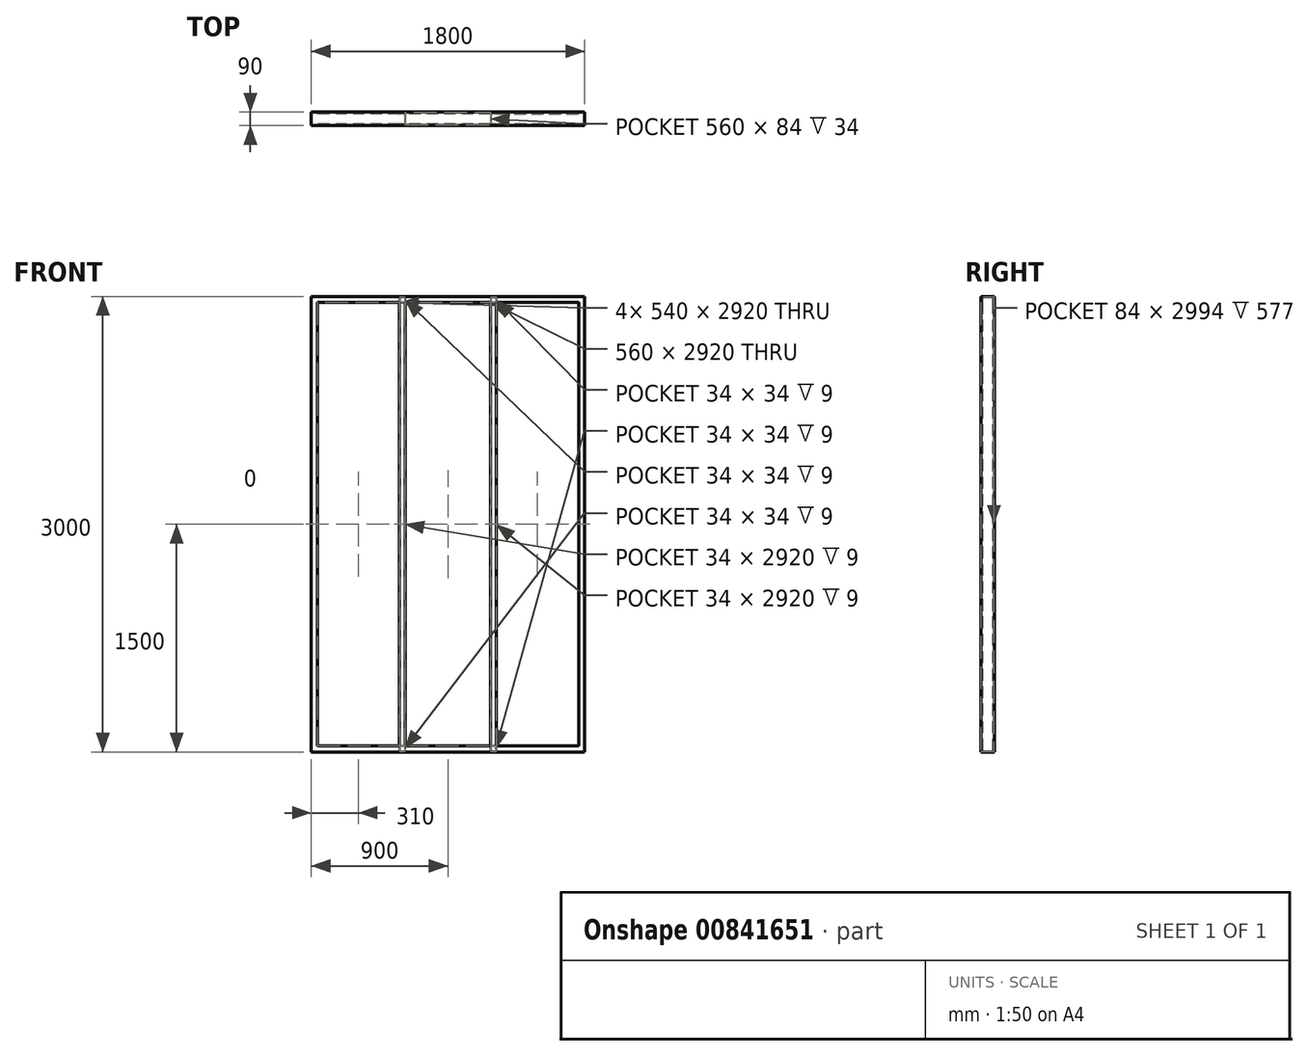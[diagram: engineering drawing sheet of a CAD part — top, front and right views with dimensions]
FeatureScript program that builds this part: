
annotation { "Feature Type Name" : "Feature", "Feature Type Description" : "" }
export const myFeature = defineFeature(function(context is Context, id is Id, definition is map)
    precondition{}
    {
        {
            var Q0;
            Q0=qCreatedBy(makeId("Front.planeOp"),FACE);
            var sketch = newSketch(context, id + "F0", { "sketchPlane" : qUnion([Q0])});
            skLineSegment(sketch, "E0.bottom", {"start": v(0, 0) * mm, "end": v(1800, 0) * mm});
            skLineSegment(sketch, "E0.top", {"start": v(0, 3000) * mm, "end": v(1800, 3000) * mm});
            skLineSegment(sketch, "E0.left", {"start": v(0, 0) * mm, "end": v(0, 3000) * mm});
            skLineSegment(sketch, "E0.right", {"start": v(1800, 0) * mm, "end": v(1800, 3000) * mm});
            skSolve(sketch);
        }
        {
            var Q0;
            Q0=qCreatedBy(makeId("Top.planeOp"),FACE);
            var sketch = newSketch(context, id + "F1", { "sketchPlane" : qUnion([Q0])});
            skLineSegment(sketch, "E1", {"start": v(0, 0) * mm, "end": v(0, -45) * mm});
            skLineSegment(sketch, "E2", {"start": v(0, -45) * mm, "end": v(40, -45) * mm});
            skLineSegment(sketch, "E3", {"start": v(40, -45) * mm, "end": v(40, -33) * mm});
            skLineSegment(sketch, "E4.MirrorCS", {"start": v(0, 0) * mm, "end": v(0, 45) * mm});
            skLineSegment(sketch, "E5.MirrorCS", {"start": v(0, 45) * mm, "end": v(40, 45) * mm});
            skLineSegment(sketch, "E6.MirrorCS", {"start": v(40, 45) * mm, "end": v(40, 33) * mm});
            skLineSegment(sketch, "E7.0", {"start": v(37, 42) * mm, "end": v(37, 33) * mm});
            skLineSegment(sketch, "E7.1", {"start": v(3, 42) * mm, "end": v(37, 42) * mm});
            skLineSegment(sketch, "E7.2", {"start": v(37, -42) * mm, "end": v(37, -33) * mm});
            skLineSegment(sketch, "E7.3", {"start": v(3, -42) * mm, "end": v(37, -42) * mm});
            skLineSegment(sketch, "E7.4", {"start": v(3, 0) * mm, "end": v(3, -42) * mm});
            skLineSegment(sketch, "E7.5", {"start": v(3, 0) * mm, "end": v(3, 42) * mm});
            skLineSegment(sketch, "E8", {"start": v(37, 33) * mm, "end": v(40, 33) * mm});
            skLineSegment(sketch, "E9", {"start": v(37, -33) * mm, "end": v(40, -33) * mm});
            skSolve(sketch);
        }
        {
            var Q0;
            Q0 = qSketchRegion(id + "F1", true);
            var Q1;
            Q1 = qConstructionFilter(qBodyType(qCreatedBy(id + "F0" ,EDGE), BodyType.WIRE), ConstructionObject.NO);
            sweep(context, id + "F2", {"profiles" : qUnion([Q0]), "path" : qUnion([Q1])});
        }
        {
            var Q0;
            Q0=qCreatedBy(makeId("Top.planeOp"),FACE);
            var sketch = newSketch(context, id + "F3", { "sketchPlane" : qUnion([Q0])});
            skLineSegment(sketch, "E10", {"start": v(580, -45) * mm, "end": v(620, -45) * mm});
            skLineSegment(sketch, "E11", {"start": v(620, -45) * mm, "end": v(620, 45) * mm});
            skLineSegment(sketch, "E12", {"start": v(620, 45) * mm, "end": v(580, 45) * mm});
            skLineSegment(sketch, "E13", {"start": v(580, 45) * mm, "end": v(580, 33) * mm});
            skLineSegment(sketch, "E14", {"start": v(580, -45) * mm, "end": v(580, -33) * mm});
            skLineSegment(sketch, "E15", {"start": v(900, -276.13) * mm, "end": v(900, 155.47) * mm, "construction": true});
            skLineSegment(sketch, "E16.MirrorCS", {"start": v(1180, -45) * mm, "end": v(1180, 45) * mm});
            skLineSegment(sketch, "E17.MirrorCS", {"start": v(1180, 45) * mm, "end": v(1220, 45) * mm});
            skLineSegment(sketch, "E18.MirrorCS", {"start": v(1220, 45) * mm, "end": v(1220, 33) * mm});
            skLineSegment(sketch, "E19.MirrorCS", {"start": v(1220, -45) * mm, "end": v(1180, -45) * mm});
            skLineSegment(sketch, "E20.MirrorCS", {"start": v(1220, -45) * mm, "end": v(1220, -33) * mm});
            skLineSegment(sketch, "E21.0", {"start": v(1795, -40) * mm, "end": v(5, -40) * mm});
            skLineSegment(sketch, "E21.1", {"start": v(1795, 40) * mm, "end": v(1795, -40) * mm});
            skLineSegment(sketch, "E21.2", {"start": v(5, 40) * mm, "end": v(1795, 40) * mm});
            skLineSegment(sketch, "E21.3", {"start": v(5, 40) * mm, "end": v(5, -40) * mm});
            skLineSegment(sketch, "E22.0", {"start": v(583, 42) * mm, "end": v(583, 33) * mm});
            skLineSegment(sketch, "E22.1", {"start": v(583, -42) * mm, "end": v(583, -33) * mm});
            skLineSegment(sketch, "E22.2", {"start": v(583, -42) * mm, "end": v(617, -42) * mm});
            skLineSegment(sketch, "E22.3", {"start": v(617, -42) * mm, "end": v(617, 42) * mm});
            skLineSegment(sketch, "E22.4", {"start": v(617, 42) * mm, "end": v(583, 42) * mm});
            skLineSegment(sketch, "E23", {"start": v(583, -33) * mm, "end": v(580, -33) * mm});
            skLineSegment(sketch, "E24", {"start": v(583, 33) * mm, "end": v(580, 33) * mm});
            skLineSegment(sketch, "E25.MirrorCS", {"start": v(1183, -42) * mm, "end": v(1183, 42) * mm});
            skLineSegment(sketch, "E26.MirrorCS", {"start": v(1183, 42) * mm, "end": v(1217, 42) * mm});
            skLineSegment(sketch, "E27.MirrorCS", {"start": v(1217, 42) * mm, "end": v(1217, 33) * mm});
            skLineSegment(sketch, "E28.MirrorCS", {"start": v(1217, 33) * mm, "end": v(1220, 33) * mm});
            skLineSegment(sketch, "E29.MirrorCS", {"start": v(1217, -42) * mm, "end": v(1183, -42) * mm});
            skLineSegment(sketch, "E30.MirrorCS", {"start": v(1217, -42) * mm, "end": v(1217, -33) * mm});
            skLineSegment(sketch, "E31.MirrorCS", {"start": v(1217, -33) * mm, "end": v(1220, -33) * mm});
            skSolve(sketch);
        }
        {
            var Q0;
            {var subQ1=sQuery(id+"F3.wireOp",EDGE,"E10");Q0=makeQuery(id+"F3.imprint","IMPRINT",FACE,{"disambiguationData":[TD([[makeQuery(id+"F3.imprint","IMPRINT",EDGE,{"derivedFrom":subQ1}),1.0]])]});}
            var Q1;
            {var subQ0=sQuery(id+"F3.wireOp",EDGE,"E21.0");var subQ1=sQuery(id+"F3.wireOp",EDGE,"E11");var subQ2=makeQuery(id+"F3.imprint","INTERSECT",VERTEX,{"derivedFrom":[subQ1,subQ0]});Q1=makeQuery(id+"F3.imprint","IMPRINT",FACE,{"disambiguationData":[TD([[makeQuery(id+"F3.imprint","IMPRINT",EDGE,{"disambiguationData":[TD([[subQ2,-1.0]])],"derivedFrom":subQ1}),1.0]])]});}
            var Q2;
            {var subQ0=sQuery(id+"F3.wireOp",EDGE,"E23");Q2=makeQuery(id+"F3.imprint","IMPRINT",FACE,{"disambiguationData":[TD([[makeQuery(id+"F3.imprint","IMPRINT",EDGE,{"derivedFrom":subQ0}),1.0]])]});}
            var Q3;
            {var subQ1=sQuery(id+"F3.wireOp",EDGE,"E12");Q3=makeQuery(id+"F3.imprint","IMPRINT",FACE,{"disambiguationData":[TD([[makeQuery(id+"F3.imprint","IMPRINT",EDGE,{"derivedFrom":subQ1}),1.0]])]});}
            var Q4;
            {var subQ0=sQuery(id+"F3.wireOp",EDGE,"E24");Q4=makeQuery(id+"F3.imprint","IMPRINT",FACE,{"disambiguationData":[TD([[makeQuery(id+"F3.imprint","IMPRINT",EDGE,{"derivedFrom":subQ0}),-1.0]])]});}
            var Q5;
            {var subQ0=sQuery(id+"F3.wireOp",EDGE,"E28.MirrorCS");Q5=makeQuery(id+"F3.imprint","IMPRINT",FACE,{"disambiguationData":[TD([[makeQuery(id+"F3.imprint","IMPRINT",EDGE,{"derivedFrom":subQ0}),1.0]])]});}
            var Q6;
            {var subQ1=sQuery(id+"F3.wireOp",EDGE,"E17.MirrorCS");Q6=makeQuery(id+"F3.imprint","IMPRINT",FACE,{"disambiguationData":[TD([[makeQuery(id+"F3.imprint","IMPRINT",EDGE,{"derivedFrom":subQ1}),-1.0]])]});}
            var Q7;
            {var subQ0=sQuery(id+"F3.wireOp",EDGE,"E21.0");var subQ1=sQuery(id+"F3.wireOp",EDGE,"E16.MirrorCS");var subQ2=makeQuery(id+"F3.imprint","INTERSECT",VERTEX,{"derivedFrom":[subQ1,subQ0]});Q7=makeQuery(id+"F3.imprint","IMPRINT",FACE,{"disambiguationData":[TD([[makeQuery(id+"F3.imprint","IMPRINT",EDGE,{"disambiguationData":[TD([[subQ2,-1.0]])],"derivedFrom":subQ1}),-1.0]])]});}
            var Q8;
            {var subQ5=sQuery(id+"F3.wireOp",EDGE,"E19.MirrorCS");Q8=makeQuery(id+"F3.imprint","IMPRINT",FACE,{"disambiguationData":[TD([[makeQuery(id+"F3.imprint","IMPRINT",EDGE,{"derivedFrom":subQ5}),-1.0]])]});}
            var Q9;
            {var subQ0=sQuery(id+"F3.wireOp",EDGE,"E31.MirrorCS");Q9=makeQuery(id+"F3.imprint","IMPRINT",FACE,{"disambiguationData":[TD([[makeQuery(id+"F3.imprint","IMPRINT",EDGE,{"derivedFrom":subQ0}),-1.0]])]});}
            var Q10;
            Q10=makeQuery(id+"F2.opSweep","SWEPT_FACE",FACE,{"disambiguationData":[OSD([sQuery(id+"F0.wireOp",EDGE,"E0.top"),sQuery(id+"F1.wireOp",EDGE,"E7.4"),sQuery(id+"F1.wireOp",EDGE,"E7.5")])]});
            extrude(context, id + "F4", {"entities" : qUnion([Q0, Q1, Q2, Q3, Q4, Q5, Q6, Q7, Q8, Q9]), "operationType" : NewBodyOperationType.ADD, "endBound" : BoundingType.UP_TO_SURFACE, "depth" : 25 * mm, "endBoundEntityFace" : qUnion([Q10]), "offsetDistance" : 25 * mm});
        }
    });
